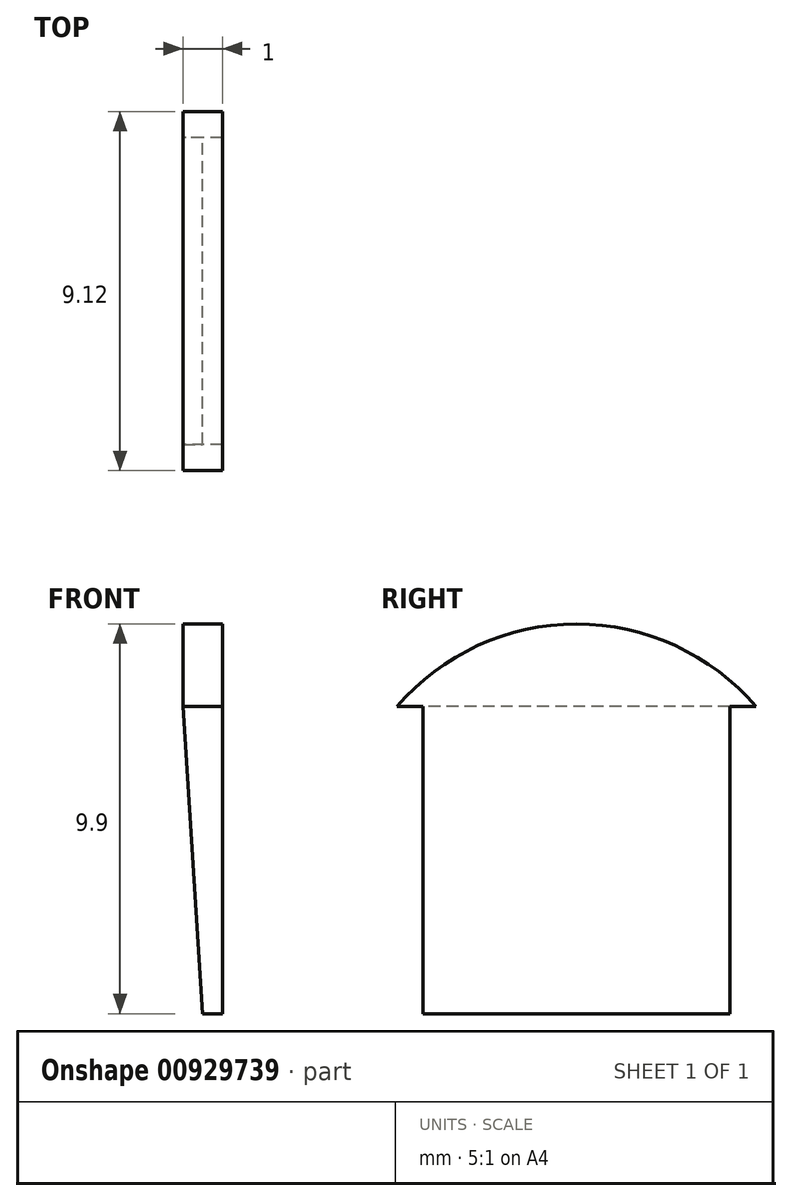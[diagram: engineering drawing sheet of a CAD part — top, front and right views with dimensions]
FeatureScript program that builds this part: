
annotation { "Feature Type Name" : "Feature", "Feature Type Description" : "" }
export const myFeature = defineFeature(function(context is Context, id is Id, definition is map)
    precondition{}
    {
        {
            var Q0;
            Q0=qCreatedBy(makeId("Right.planeOp"),FACE);
            var sketch = newSketch(context, id + "F0", { "sketchPlane" : qUnion([Q0])});
            skLineSegment(sketch, "E0.bottom", {"start": v(3.9, -6.38) * mm, "end": v(-3.9, -6.38) * mm});
            skLineSegment(sketch, "E0.top", {"start": v(3.9, 1.42) * mm, "end": v(-3.9, 1.42) * mm});
            skLineSegment(sketch, "E0.left", {"start": v(3.9, -6.38) * mm, "end": v(3.9, 1.42) * mm});
            skLineSegment(sketch, "E0.right", {"start": v(-3.9, -6.38) * mm, "end": v(-3.9, 1.42) * mm});
            skPoint(sketch, "E0.middle", {"position": v(0, -2.48) * mm});
            skLineSegment(sketch, "E1", {"start": v(-6, 1.42) * mm, "end": v(-5.07, 1.42) * mm, "construction": true});
            skLineSegment(sketch, "E2", {"start": v(3.9, 1.42) * mm, "end": v(4.56, 1.42) * mm});
            skLineSegment(sketch, "E3", {"start": v(-3.9, 1.42) * mm, "end": v(-5.07, 1.42) * mm});
            skArc(sketch, "E4", {"start": v(4.56, 1.42) * mm, "mid": v(0, 3.52) * mm, "end": v(-4.56, 1.42) * mm});
            skLineSegment(sketch, "E5.trimOffspring", {"start": v(-4.56, 1.42) * mm, "end": v(-3.9, 1.42) * mm, "construction": true});
            skSolve(sketch);
        }
        {
            var Q0;
            Q0=makeQuery(id+"F0.imprint","IMPRINT",FACE,{"disambiguationData":[TD([[makeQuery(id+"F0.imprint","IMPRINT",EDGE,{"derivedFrom":sQuery(id+"F0.wireOp",EDGE,"E0.top")}),-1.0]])]});
            var Q1;
            Q1=makeQuery(id+"F0.imprint","IMPRINT",FACE,{"disambiguationData":[TD([[makeQuery(id+"F0.imprint","IMPRINT",EDGE,{"derivedFrom":sQuery(id+"F0.wireOp",EDGE,"E0.bottom")}),-1.0]])]});
            var Q2;
            {var subQ0=sQuery(id+"F0.wireOp",EDGE,"E0.left");var subQ3=sQuery(id+"F0.wireOp",EDGE,"b0ba94fa-534d-4b90-9c10-640092ca653e.0");var subQ5=makeQuery(id+"F0.imprint","INTERSECT",VERTEX,{"derivedFrom":[subQ0,subQ3]});Q2=makeQuery(id+"F0.imprint","IMPRINT",FACE,{"disambiguationData":[TD([[makeQuery(id+"F0.imprint","IMPRINT",EDGE,{"disambiguationData":[TD([[subQ5,-1.0]])],"derivedFrom":subQ3}),-1.0]])]});}
            var Q3;
            {var subQ0=sQuery(id+"F0.wireOp",EDGE,"b0ba94fa-534d-4b90-9c10-640092ca653e.0");var subQ1=sQuery(id+"F0.wireOp",EDGE,"E0.top");var subQ2=makeQuery(id+"F0.imprint","INTERSECT",VERTEX,{"disambiguationData":[OD(0.0)],"derivedFrom":[subQ1,subQ0]});Q3=makeQuery(id+"F0.imprint","IMPRINT",FACE,{"disambiguationData":[TD([[makeQuery(id+"F0.imprint","IMPRINT",EDGE,{"disambiguationData":[TD([[subQ2,-1.0]])],"derivedFrom":subQ1}),-1.0]])]});}
            var Q4;
            {var subQ0=sQuery(id+"F0.wireOp",EDGE,"E0.right");var subQ3=sQuery(id+"F0.wireOp",EDGE,"b0ba94fa-534d-4b90-9c10-640092ca653e.0");var subQ5=makeQuery(id+"F0.imprint","INTERSECT",VERTEX,{"derivedFrom":[subQ0,subQ3]});Q4=makeQuery(id+"F0.imprint","IMPRINT",FACE,{"disambiguationData":[TD([[makeQuery(id+"F0.imprint","IMPRINT",EDGE,{"disambiguationData":[TD([[subQ5,1.0]])],"derivedFrom":subQ3}),-1.0]])]});}
            extrude(context, id + "F1", {"entities" : qUnion([Q0, Q1, Q2, Q3, Q4]), "depth" : 1 * mm, "offsetDistance" : 25 * mm});
        }
        {
            var Q0;
            Q0=makeQuery(id+"F1.opExtrude","CAP_EDGE",EDGE,{"disambiguationData":[OSD([sQuery(id+"F0.wireOp",EDGE,"E0.bottom")])],"isStart":true});
            chamfer(context, id + "F2", {"entities" : qUnion([Q0]), "chamferType" : ChamferType.TWO_OFFSETS, "width1" : 7.8 * mm, "oppositeDirection" : false, "width2" : 0.5 * mm, "tangentPropagation" : true});
        }
    });
